# Revit family: Enave_100_Eng
name_source: partatom
category: Оборудование
units: mm (PartAtom-declared; Revit-internal decimal feet)

## family parameters
Всегда вертикально = Да
Классификация = Нет
На основе рабочей плоскости = Нет
Общий = Нет
При загрузке вырезать с полостями = Нет
Размер круглого соединителя = Использовать диаметр
Тип детали = Нормальный
Точка принадлежности помещению = Нет

## types (2) — shared parameters
00_20_Manufacturer = Vents
00_20_Name = Air handling units with heat recovery
Amperage = 0 А
Casing Material = Polypropylene (black)
D = 125 мм
Diameter = 125 мм
Filter = G4 / Coarse > 60%
H = 242 мм
Height = 242 мм
L = 530 мм
Length = 530 мм
Load Classification = HVAC
Maintenance zone material = <По категории>
Maximum Air Flow = 130.0 м³/ч
Number of Fase = 1
Power = 38 Вт
Sound pressure level at 3 m distance = 32 дБА
URL = https://ventilation-system.com
Voltage = 230 В
W = 520 мм
Weight = 8.00 кг
Width = 520 мм
d = 115 мм
l = 420 мм
w = 410 мм
Изготовитель = Vents
zero-valued in all types: Отметка по умолчанию

## type names (no varying parameters)
- Enave-C 100 P А14
- Enave-CT 100 P А14

note: column(s) folded — value = type name in every type: 00_20_Type
